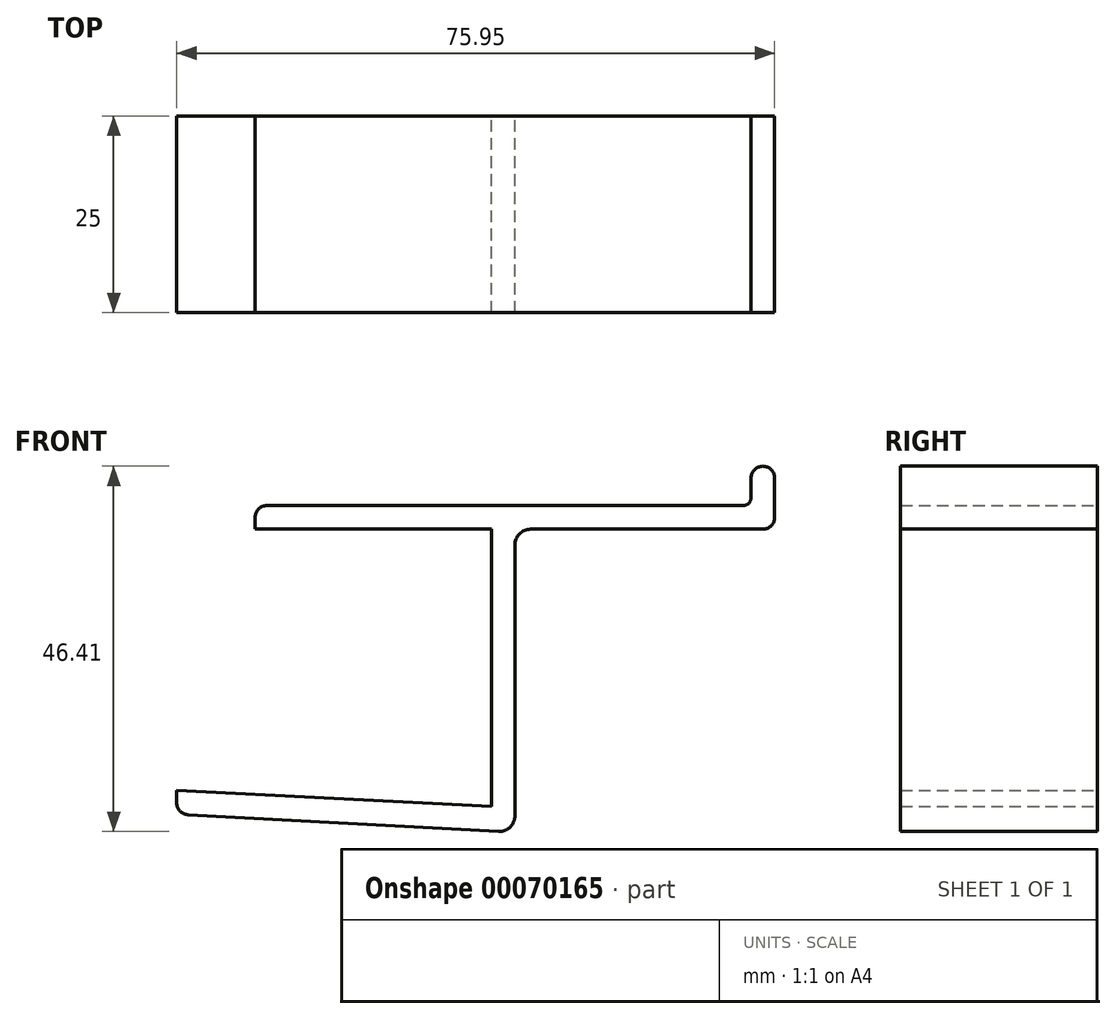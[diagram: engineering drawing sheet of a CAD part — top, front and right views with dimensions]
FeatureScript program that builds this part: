
annotation { "Feature Type Name" : "Feature", "Feature Type Description" : "" }
export const myFeature = defineFeature(function(context is Context, id is Id, definition is map)
    precondition{}
    {
        {
            var Q0;
            Q0=qCreatedBy(makeId("Front.planeOp"),FACE);
            var sketch = newSketch(context, id + "F0", { "sketchPlane" : qUnion([Q0])});
            skLineSegment(sketch, "E0", {"start": v(-31.5, 33.45) * mm, "end": v(29, 33.45) * mm});
            skLineSegment(sketch, "E1", {"start": v(30, 34.45) * mm, "end": v(30, 36.95) * mm});
            skLineSegment(sketch, "E2", {"start": v(31.5, 38.45) * mm, "end": v(31.5, 38.45) * mm});
            skLineSegment(sketch, "E3", {"start": v(33, 36.95) * mm, "end": v(33, 31.95) * mm});
            skLineSegment(sketch, "E4", {"start": v(31.5, 30.45) * mm, "end": v(2, 30.45) * mm});
            skLineSegment(sketch, "E5", {"start": v(0, 28.45) * mm, "end": v(0, -5.96) * mm});
            skLineSegment(sketch, "E6", {"start": v(-2.1, -7.96) * mm, "end": v(-41.53, -5.83) * mm});
            skLineSegment(sketch, "E7", {"start": v(-42.95, -4.33) * mm, "end": v(-42.95, -2.75) * mm});
            skLineSegment(sketch, "E8", {"start": v(-42.95, -2.75) * mm, "end": v(-3, -4.75) * mm});
            skLineSegment(sketch, "E9", {"start": v(-3, -4.75) * mm, "end": v(-3, 30.45) * mm});
            skLineSegment(sketch, "E10", {"start": v(-3, 30.45) * mm, "end": v(-33, 30.45) * mm});
            skLineSegment(sketch, "E11", {"start": v(-33, 30.45) * mm, "end": v(-33, 31.95) * mm});
            skPoint(sketch, "E12.visualSharp", {"position": v(33, 30.45) * mm});
            skArc(sketch, "E12.filletArc", {"start": v(31.5, 30.45) * mm, "mid": v(32.56, 30.9) * mm, "end": v(33, 31.95) * mm});
            skPoint(sketch, "E13.visualSharp", {"position": v(30, 33.45) * mm});
            skArc(sketch, "E13.filletArc", {"start": v(29, 33.45) * mm, "mid": v(29.7, 33.74) * mm, "end": v(30, 34.45) * mm});
            skPoint(sketch, "E14.visualSharp", {"position": v(33, 38.45) * mm});
            skArc(sketch, "E14.filletArc", {"start": v(33, 36.95) * mm, "mid": v(32.56, 38.01) * mm, "end": v(31.5, 38.45) * mm});
            skPoint(sketch, "E15.visualSharp", {"position": v(30, 38.45) * mm});
            skArc(sketch, "E15.filletArc", {"start": v(31.5, 38.45) * mm, "mid": v(30.44, 38.01) * mm, "end": v(30, 36.95) * mm});
            skPoint(sketch, "E16.visualSharp", {"position": v(-42.95, -5.75) * mm});
            skArc(sketch, "E16.filletArc", {"start": v(-42.95, -4.33) * mm, "mid": v(-42.54, -5.36) * mm, "end": v(-41.53, -5.83) * mm});
            skPoint(sketch, "E17.visualSharp", {"position": v(0, -8.07) * mm});
            skArc(sketch, "E17.filletArc", {"start": v(-2.1, -7.96) * mm, "mid": v(-0.62, -7.41) * mm, "end": v(0, -5.96) * mm});
            skPoint(sketch, "E18.visualSharp", {"position": v(0, 30.45) * mm});
            skArc(sketch, "E18.filletArc", {"start": v(2, 30.45) * mm, "mid": v(0.59, 29.87) * mm, "end": v(0, 28.45) * mm});
            skPoint(sketch, "E19.visualSharp", {"position": v(-33, 33.45) * mm});
            skArc(sketch, "E19.filletArc", {"start": v(-31.5, 33.45) * mm, "mid": v(-32.56, 33.01) * mm, "end": v(-33, 31.95) * mm});
            skSolve(sketch);
        }
        {
            var Q0;
            Q0=makeQuery(id+"F0.imprint","IMPRINT",FACE,{"disambiguationData":[TD([[makeQuery(id+"F0.imprint","IMPRINT",EDGE,{"derivedFrom":sQuery(id+"F0.wireOp",EDGE,"E0")}),-1.0]])]});
            extrude(context, id + "F1", {"entities" : qUnion([Q0]), "depth" : 25 * mm});
        }
    });
